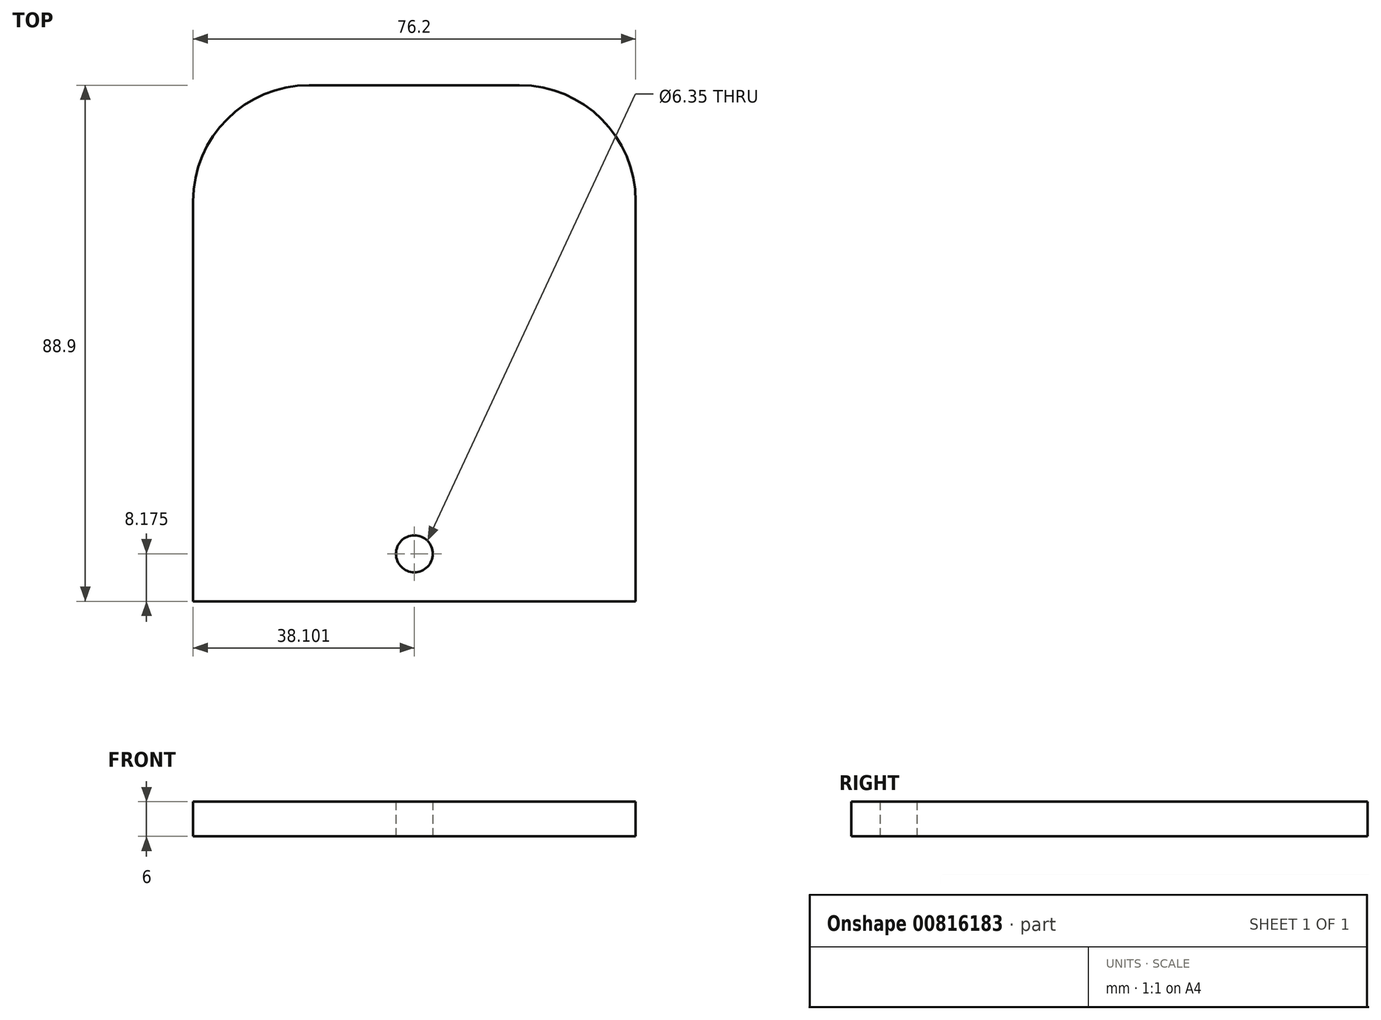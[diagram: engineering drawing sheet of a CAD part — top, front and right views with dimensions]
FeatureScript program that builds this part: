
annotation { "Feature Type Name" : "Feature", "Feature Type Description" : "" }
export const myFeature = defineFeature(function(context is Context, id is Id, definition is map)
    precondition{}
    {
        {
            var Q0;
            Q0=qCreatedBy(makeId("Top.planeOp"),FACE);
            var sketch = newSketch(context, id + "F0", { "sketchPlane" : qUnion([Q0])});
            skLineSegment(sketch, "E0.bottom", {"start": v(-21.73, -28.24) * mm, "end": v(-97.93, -28.24) * mm});
            skLineSegment(sketch, "E0.top", {"start": v(-41.73, 60.66) * mm, "end": v(-77.93, 60.66) * mm});
            skLineSegment(sketch, "E0.left", {"start": v(-21.73, -28.24) * mm, "end": v(-21.73, 40.66) * mm});
            skLineSegment(sketch, "E0.right", {"start": v(-97.93, -28.24) * mm, "end": v(-97.93, 40.66) * mm});
            skPoint(sketch, "E0.middle", {"position": v(-59.83, 16.2) * mm});
            skPoint(sketch, "E1.visualSharp", {"position": v(-97.93, 60.66) * mm});
            skArc(sketch, "E1.filletArc", {"start": v(-77.93, 60.66) * mm, "mid": v(-92.07, 54.8) * mm, "end": v(-97.93, 40.66) * mm});
            skPoint(sketch, "E2.visualSharp", {"position": v(-21.73, 60.66) * mm});
            skArc(sketch, "E2.filletArc", {"start": v(-21.73, 40.66) * mm, "mid": v(-27.59, 54.8) * mm, "end": v(-41.73, 60.66) * mm});
            skLineSegment(sketch, "E3", {"start": v(-59.83, 60.66) * mm, "end": v(-59.83, -28.24) * mm, "construction": true});
            skLineSegment(sketch, "E4", {"start": v(-21.73, 16.2) * mm, "end": v(-97.93, 16.2) * mm, "construction": true});
            skLineSegment(sketch, "E5.MirrorCS", {"start": v(-97.93, 16.2) * mm, "end": v(-21.73, 16.2) * mm, "construction": true});
            skArc(sketch, "E6.MirrorCS", {"start": v(-41.73, 60.66) * mm, "mid": v(-27.59, 54.8) * mm, "end": v(-21.73, 40.66) * mm});
            skCircle(sketch, "E7", {"center": v(-59.83, -20.07) * mm, "radius": 3.17 * mm});
            skSolve(sketch);
        }
        {
            var Q0;
            Q0 = qSketchRegion(id + "F0", true);
            extrude(context, id + "F1", {"entities" : qUnion([Q0]), "endBound" : BoundingType.SYMMETRIC, "depth" : 6 * mm, "offsetDistance" : 25 * mm});
        }
    });
